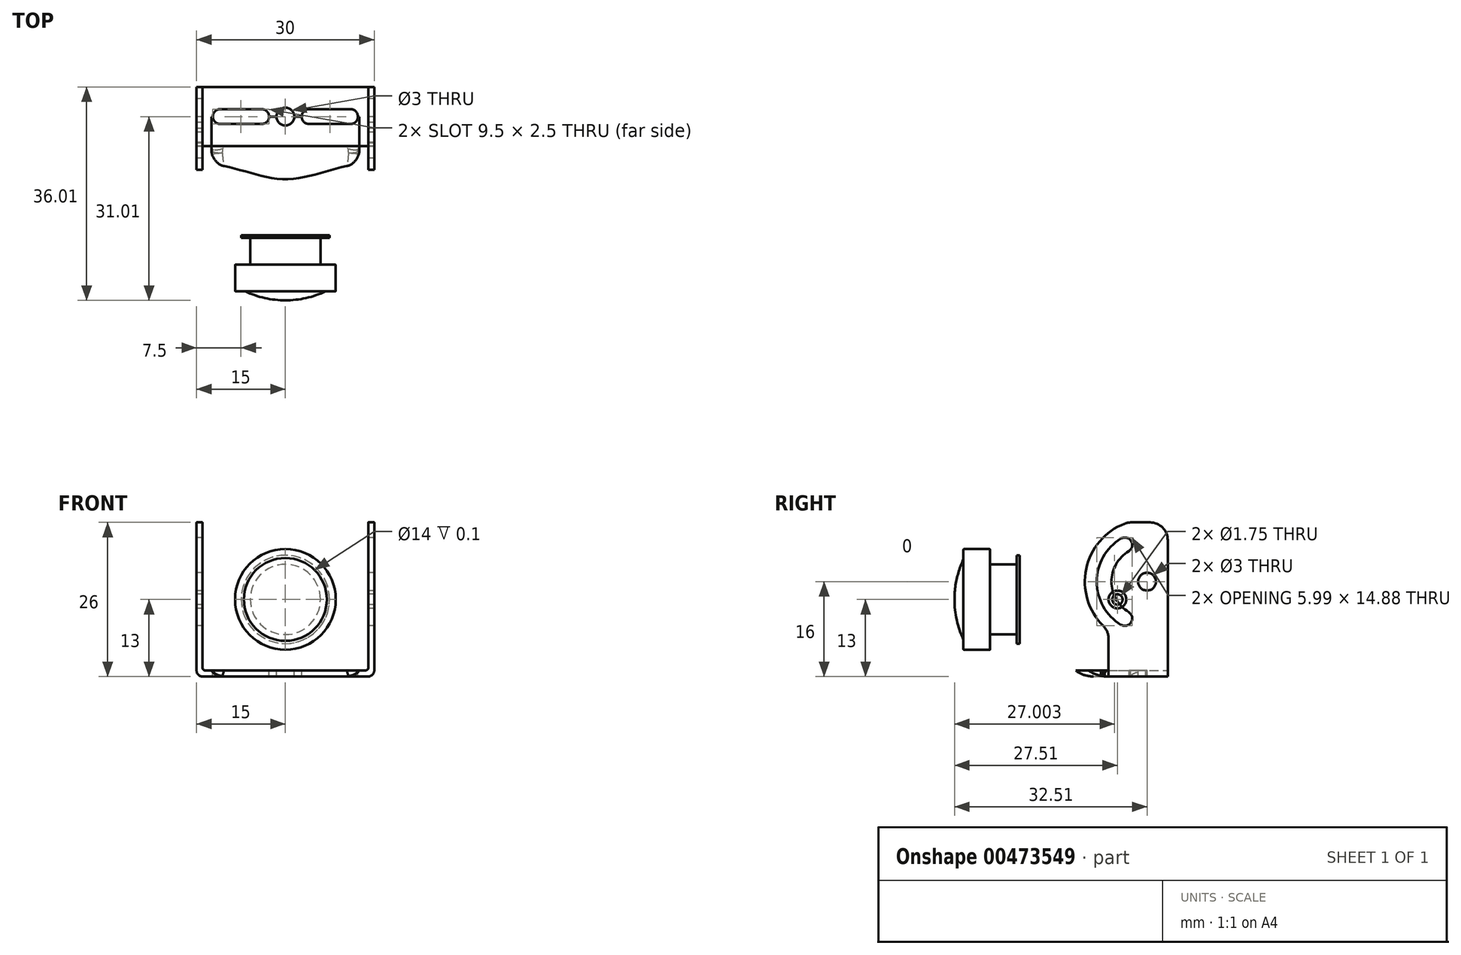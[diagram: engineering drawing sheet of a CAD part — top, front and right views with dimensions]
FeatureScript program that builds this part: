
annotation { "Feature Type Name" : "Feature", "Feature Type Description" : "" }
export const myFeature = defineFeature(function(context is Context, id is Id, definition is map)
    precondition{}
    {
        {
            var Q0;
            Q0=qCreatedBy(makeId("Right.planeOp"),FACE);
            var sketch = newSketch(context, id + "F0", { "sketchPlane" : qUnion([Q0])});
            skLineSegment(sketch, "E0", {"start": v(-18.38, 0) * mm, "end": v(-1.77, 16.62) * mm, "construction": true});
            skLineSegment(sketch, "E1", {"start": v(1.77, 16.62) * mm, "end": v(18.38, 0) * mm, "construction": true});
            skLineSegment(sketch, "E2", {"start": v(18.38, 0) * mm, "end": v(0, -18.38) * mm, "construction": true});
            skLineSegment(sketch, "E3", {"start": v(0, -18.38) * mm, "end": v(-18.38, 0) * mm, "construction": true});
            skArc(sketch, "E4", {"start": v(-5.5, 17.35) * mm, "mid": v(-8.56, 16.3) * mm, "end": v(-10.34, 13.6) * mm});
            skLineSegment(sketch, "E5", {"start": v(-17, 0) * mm, "end": v(-17, 7.32) * mm});
            skArc(sketch, "E6", {"start": v(-16.59, 7.81) * mm, "mid": v(-12.62, 9.8) * mm, "end": v(-10.34, 13.6) * mm});
            skLineSegment(sketch, "E7", {"start": v(0, 0) * mm, "end": v(-17, 0) * mm});
            skPoint(sketch, "E8.visualSharp", {"position": v(0, 18.38) * mm});
            skArc(sketch, "E8.filletArc", {"start": v(1.77, 16.62) * mm, "mid": v(0, 17.35) * mm, "end": v(-1.77, 16.62) * mm, "construction": true});
            skLineSegment(sketch, "E9", {"start": v(0, 17.35) * mm, "end": v(0, 0) * mm});
            skLineSegment(sketch, "E10", {"start": v(0, 17.35) * mm, "end": v(-5.5, 17.35) * mm});
            skPoint(sketch, "E11.visualSharp", {"position": v(-17, 7.75) * mm});
            skArc(sketch, "E11.filletArc", {"start": v(-16.59, 7.81) * mm, "mid": v(-16.88, 7.64) * mm, "end": v(-17, 7.32) * mm});
            skSolve(sketch);
        }
        {
            var Q0;
            Q0=qCreatedBy(makeId("Front.planeOp"),FACE);
            var sketch = newSketch(context, id + "F1", { "sketchPlane" : qUnion([Q0])});
            skLineSegment(sketch, "E12.bottom", {"start": v(10.5, 13) * mm, "end": v(-10.5, 13) * mm});
            skLineSegment(sketch, "E12.top", {"start": v(10.5, -13) * mm, "end": v(-10.5, -13) * mm});
            skLineSegment(sketch, "E12.left", {"start": v(13, 10.5) * mm, "end": v(13, -10.5) * mm});
            skLineSegment(sketch, "E12.right", {"start": v(-13, 10.5) * mm, "end": v(-13, -10.5) * mm});
            skPoint(sketch, "E13.visualSharp", {"position": v(13, 13) * mm});
            skArc(sketch, "E13.filletArc", {"start": v(13, 10.5) * mm, "mid": v(12.27, 12.27) * mm, "end": v(10.5, 13) * mm});
            skPoint(sketch, "E14.visualSharp", {"position": v(-13, 13) * mm});
            skArc(sketch, "E14.filletArc", {"start": v(-10.5, 13) * mm, "mid": v(-12.27, 12.27) * mm, "end": v(-13, 10.5) * mm});
            skPoint(sketch, "E15.visualSharp", {"position": v(13, -13) * mm});
            skArc(sketch, "E15.filletArc", {"start": v(10.5, -13) * mm, "mid": v(12.27, -12.27) * mm, "end": v(13, -10.5) * mm});
            skPoint(sketch, "E16.visualSharp", {"position": v(-13, -13) * mm});
            skArc(sketch, "E16.filletArc", {"start": v(-13, -10.5) * mm, "mid": v(-12.27, -12.27) * mm, "end": v(-10.5, -13) * mm});
            skLineSegment(sketch, "E17.bottom", {"start": v(20, 20) * mm, "end": v(-20, 20) * mm});
            skLineSegment(sketch, "E17.top", {"start": v(20, -20) * mm, "end": v(-20, -20) * mm});
            skLineSegment(sketch, "E17.left", {"start": v(20, 20) * mm, "end": v(20, -20) * mm});
            skLineSegment(sketch, "E17.right", {"start": v(-20, 20) * mm, "end": v(-20, -20) * mm});
            skSolve(sketch);
        }
        {
            var Q0;
            Q0=makeQuery(id+"F0.imprint","IMPRINT",FACE,{"disambiguationData":[TD([[makeQuery(id+"F0.imprint","IMPRINT",EDGE,{"derivedFrom":sQuery(id+"F0.wireOp",EDGE,"E4")}),1.0]])]});
            var Q1;
            Q1=sQuery(id+"F0.wireOp",EDGE,"E7");
            revolve(context, id + "F2", {"entities" : qUnion([Q0]), "axis" : qUnion([Q1]), "revolveType" : RevolveType.FULL});
        }
        {
            var Q0;
            Q0=qSketchRegion(id+"F1",true);
            extrude(context, id + "F3", {"entities" : qUnion([Q0]), "operationType" : NewBodyOperationType.REMOVE, "depth" : 25 * mm});
        }
        {
            var Q0;
            Q0=makeQuery(id+"F3.boolean.opBoolean","INTERSECT",EDGE,{"derivedFrom":[makeQuery(id+"F2.opRevolve","SWEPT_FACE",FACE,{"disambiguationData":[OSD([sQuery(id+"F0.wireOp",EDGE,"E6")])]}),makeQuery(id+"F3.opExtrude","SWEPT_FACE",FACE,{"disambiguationData":[OSD([sQuery(id+"F1.wireOp",EDGE,"E12.left")])]})]});
            var Q1;
            Q1=makeQuery(id+"F3.boolean.opBoolean","INTERSECT",EDGE,{"derivedFrom":[makeQuery(id+"F2.opRevolve","SWEPT_FACE",FACE,{"disambiguationData":[OSD([sQuery(id+"F0.wireOp",EDGE,"E6")])]}),makeQuery(id+"F3.opExtrude","SWEPT_FACE",FACE,{"disambiguationData":[OSD([sQuery(id+"F1.wireOp",EDGE,"E12.top")])]})]});
            var Q2;
            Q2=makeQuery(id+"F3.boolean.opBoolean","INTERSECT",EDGE,{"derivedFrom":[makeQuery(id+"F2.opRevolve","SWEPT_FACE",FACE,{"disambiguationData":[OSD([sQuery(id+"F0.wireOp",EDGE,"E6")])]}),makeQuery(id+"F3.opExtrude","SWEPT_FACE",FACE,{"disambiguationData":[OSD([sQuery(id+"F1.wireOp",EDGE,"E12.right")])]})]});
            var Q3;
            Q3=makeQuery(id+"F3.boolean.opBoolean","INTERSECT",EDGE,{"derivedFrom":[makeQuery(id+"F2.opRevolve","SWEPT_FACE",FACE,{"disambiguationData":[OSD([sQuery(id+"F0.wireOp",EDGE,"E6")])]}),makeQuery(id+"F3.opExtrude","SWEPT_FACE",FACE,{"disambiguationData":[OSD([sQuery(id+"F1.wireOp",EDGE,"E12.bottom")])]})]});
            fillet(context, id + "F4", {"entities" : qUnion([Q0, Q1, Q2, Q3]), "radius" : 5 * mm, "allowEdgeOverflow" : false});
        }
        {
            var Q0;
            {var subQ0=makeQuery(id+"F2.opRevolve","SWEPT_FACE",FACE,{"disambiguationData":[OSD([sQuery(id+"F0.wireOp",EDGE,"E6")])]});var subQ1=makeQuery(id+"F3.opExtrude","SWEPT_FACE",FACE,{"disambiguationData":[OSD([sQuery(id+"F1.wireOp",EDGE,"E12.top")])]});Q0=makeQuery(id+"F4.opFillet","BLEND_EDGE",EDGE,{"blendedFrom":[makeQuery(id+"F3.boolean.opBoolean","INTERSECT",EDGE,{"derivedFrom":[subQ0,subQ1]}),makeQuery(id+"F3.boolean.opBoolean","SPLIT",FACE,{"disambiguationData":[TD([makeQuery(id+"F3.opExtrude","SWEPT_FACE",FACE,{"disambiguationData":[OSD([sQuery(id+"F1.wireOp",EDGE,"E16.filletArc")])]})])],"derivedFrom":makeQuery(id+"F2.opRevolve","SWEPT_FACE",FACE,{"disambiguationData":[OSD([sQuery(id+"F0.wireOp",EDGE,"E4")])]})})],"blendedInto":[makeQuery(id+"F3.boolean.opBoolean","SPLIT",FACE,{"disambiguationData":[TD([makeQuery(id+"F3.opExtrude","SWEPT_FACE",FACE,{"disambiguationData":[OSD([sQuery(id+"F1.wireOp",EDGE,"E16.filletArc")])]})])],"derivedFrom":makeQuery(id+"F2.opRevolve","SWEPT_FACE",FACE,{"disambiguationData":[OSD([sQuery(id+"F0.wireOp",EDGE,"E4")])]})})]});}
            var Q1;
            {var subQ0=makeQuery(id+"F2.opRevolve","SWEPT_FACE",FACE,{"disambiguationData":[OSD([sQuery(id+"F0.wireOp",EDGE,"E6")])]});var subQ1=makeQuery(id+"F3.opExtrude","SWEPT_FACE",FACE,{"disambiguationData":[OSD([sQuery(id+"F1.wireOp",EDGE,"E12.right")])]});Q1=makeQuery(id+"F4.opFillet","BLEND_EDGE",EDGE,{"blendedFrom":[makeQuery(id+"F3.boolean.opBoolean","INTERSECT",EDGE,{"derivedFrom":[subQ0,subQ1]}),makeQuery(id+"F3.boolean.opBoolean","SPLIT",FACE,{"disambiguationData":[TD([makeQuery(id+"F3.opExtrude","SWEPT_FACE",FACE,{"disambiguationData":[OSD([sQuery(id+"F1.wireOp",EDGE,"E16.filletArc")])]})])],"derivedFrom":makeQuery(id+"F2.opRevolve","SWEPT_FACE",FACE,{"disambiguationData":[OSD([sQuery(id+"F0.wireOp",EDGE,"E4")])]})})],"blendedInto":[makeQuery(id+"F3.boolean.opBoolean","SPLIT",FACE,{"disambiguationData":[TD([makeQuery(id+"F3.opExtrude","SWEPT_FACE",FACE,{"disambiguationData":[OSD([sQuery(id+"F1.wireOp",EDGE,"E16.filletArc")])]})])],"derivedFrom":makeQuery(id+"F2.opRevolve","SWEPT_FACE",FACE,{"disambiguationData":[OSD([sQuery(id+"F0.wireOp",EDGE,"E4")])]})})]});}
            var Q2;
            {var subQ0=makeQuery(id+"F2.opRevolve","SWEPT_FACE",FACE,{"disambiguationData":[OSD([sQuery(id+"F0.wireOp",EDGE,"E6")])]});Q2=makeQuery(id+"F4.opFillet","BLEND_EDGE",EDGE,{"blendedFrom":[makeQuery(id+"F3.boolean.opBoolean","INTERSECT",EDGE,{"derivedFrom":[subQ0,makeQuery(id+"F3.opExtrude","SWEPT_FACE",FACE,{"disambiguationData":[OSD([sQuery(id+"F1.wireOp",EDGE,"E12.top")])]})]}),makeQuery(id+"F3.boolean.opBoolean","INTERSECT",EDGE,{"derivedFrom":[subQ0,makeQuery(id+"F3.opExtrude","SWEPT_FACE",FACE,{"disambiguationData":[OSD([sQuery(id+"F1.wireOp",EDGE,"E12.right")])]})]})],"blendedInto":[]});}
            var Q3;
            {var subQ0=makeQuery(id+"F2.opRevolve","SWEPT_FACE",FACE,{"disambiguationData":[OSD([sQuery(id+"F0.wireOp",EDGE,"E6")])]});Q3=makeQuery(id+"F4.opFillet","BLEND_EDGE",EDGE,{"blendedFrom":[makeQuery(id+"F3.boolean.opBoolean","INTERSECT",EDGE,{"derivedFrom":[subQ0,makeQuery(id+"F3.opExtrude","SWEPT_FACE",FACE,{"disambiguationData":[OSD([sQuery(id+"F1.wireOp",EDGE,"E12.bottom")])]})]}),makeQuery(id+"F3.boolean.opBoolean","INTERSECT",EDGE,{"derivedFrom":[subQ0,makeQuery(id+"F3.opExtrude","SWEPT_FACE",FACE,{"disambiguationData":[OSD([sQuery(id+"F1.wireOp",EDGE,"E12.right")])]})]})],"blendedInto":[]});}
            var Q4;
            {var subQ0=makeQuery(id+"F2.opRevolve","SWEPT_FACE",FACE,{"disambiguationData":[OSD([sQuery(id+"F0.wireOp",EDGE,"E6")])]});var subQ1=makeQuery(id+"F3.opExtrude","SWEPT_FACE",FACE,{"disambiguationData":[OSD([sQuery(id+"F1.wireOp",EDGE,"E12.right")])]});Q4=makeQuery(id+"F4.opFillet","BLEND_EDGE",EDGE,{"blendedFrom":[makeQuery(id+"F3.boolean.opBoolean","INTERSECT",EDGE,{"derivedFrom":[subQ0,subQ1]}),makeQuery(id+"F3.boolean.opBoolean","SPLIT",FACE,{"disambiguationData":[TD([makeQuery(id+"F3.opExtrude","SWEPT_FACE",FACE,{"disambiguationData":[OSD([sQuery(id+"F1.wireOp",EDGE,"E14.filletArc")])]})])],"derivedFrom":makeQuery(id+"F2.opRevolve","SWEPT_FACE",FACE,{"disambiguationData":[OSD([sQuery(id+"F0.wireOp",EDGE,"E4")])]})})],"blendedInto":[makeQuery(id+"F3.boolean.opBoolean","SPLIT",FACE,{"disambiguationData":[TD([makeQuery(id+"F3.opExtrude","SWEPT_FACE",FACE,{"disambiguationData":[OSD([sQuery(id+"F1.wireOp",EDGE,"E14.filletArc")])]})])],"derivedFrom":makeQuery(id+"F2.opRevolve","SWEPT_FACE",FACE,{"disambiguationData":[OSD([sQuery(id+"F0.wireOp",EDGE,"E4")])]})})]});}
            var Q5;
            {var subQ0=makeQuery(id+"F2.opRevolve","SWEPT_FACE",FACE,{"disambiguationData":[OSD([sQuery(id+"F0.wireOp",EDGE,"E6")])]});var subQ1=makeQuery(id+"F3.opExtrude","SWEPT_FACE",FACE,{"disambiguationData":[OSD([sQuery(id+"F1.wireOp",EDGE,"E12.bottom")])]});Q5=makeQuery(id+"F4.opFillet","BLEND_EDGE",EDGE,{"blendedFrom":[makeQuery(id+"F3.boolean.opBoolean","INTERSECT",EDGE,{"derivedFrom":[subQ0,subQ1]}),makeQuery(id+"F3.boolean.opBoolean","SPLIT",FACE,{"disambiguationData":[TD([makeQuery(id+"F3.opExtrude","SWEPT_FACE",FACE,{"disambiguationData":[OSD([sQuery(id+"F1.wireOp",EDGE,"E14.filletArc")])]})])],"derivedFrom":makeQuery(id+"F2.opRevolve","SWEPT_FACE",FACE,{"disambiguationData":[OSD([sQuery(id+"F0.wireOp",EDGE,"E4")])]})})],"blendedInto":[makeQuery(id+"F3.boolean.opBoolean","SPLIT",FACE,{"disambiguationData":[TD([makeQuery(id+"F3.opExtrude","SWEPT_FACE",FACE,{"disambiguationData":[OSD([sQuery(id+"F1.wireOp",EDGE,"E14.filletArc")])]})])],"derivedFrom":makeQuery(id+"F2.opRevolve","SWEPT_FACE",FACE,{"disambiguationData":[OSD([sQuery(id+"F0.wireOp",EDGE,"E4")])]})})]});}
            var Q6;
            {var subQ0=makeQuery(id+"F2.opRevolve","SWEPT_FACE",FACE,{"disambiguationData":[OSD([sQuery(id+"F0.wireOp",EDGE,"E6")])]});var subQ1=makeQuery(id+"F3.opExtrude","SWEPT_FACE",FACE,{"disambiguationData":[OSD([sQuery(id+"F1.wireOp",EDGE,"E12.bottom")])]});Q6=makeQuery(id+"F4.opFillet","BLEND_EDGE",EDGE,{"blendedFrom":[makeQuery(id+"F3.boolean.opBoolean","INTERSECT",EDGE,{"derivedFrom":[subQ0,subQ1]}),makeQuery(id+"F3.boolean.opBoolean","SPLIT",FACE,{"disambiguationData":[TD([makeQuery(id+"F3.opExtrude","SWEPT_FACE",FACE,{"disambiguationData":[OSD([sQuery(id+"F1.wireOp",EDGE,"E13.filletArc")])]})])],"derivedFrom":makeQuery(id+"F2.opRevolve","SWEPT_FACE",FACE,{"disambiguationData":[OSD([sQuery(id+"F0.wireOp",EDGE,"E4")])]})})],"blendedInto":[makeQuery(id+"F3.boolean.opBoolean","SPLIT",FACE,{"disambiguationData":[TD([makeQuery(id+"F3.opExtrude","SWEPT_FACE",FACE,{"disambiguationData":[OSD([sQuery(id+"F1.wireOp",EDGE,"E13.filletArc")])]})])],"derivedFrom":makeQuery(id+"F2.opRevolve","SWEPT_FACE",FACE,{"disambiguationData":[OSD([sQuery(id+"F0.wireOp",EDGE,"E4")])]})})]});}
            var Q7;
            {var subQ0=makeQuery(id+"F2.opRevolve","SWEPT_FACE",FACE,{"disambiguationData":[OSD([sQuery(id+"F0.wireOp",EDGE,"E6")])]});var subQ1=makeQuery(id+"F3.opExtrude","SWEPT_FACE",FACE,{"disambiguationData":[OSD([sQuery(id+"F1.wireOp",EDGE,"E12.left")])]});Q7=makeQuery(id+"F4.opFillet","BLEND_EDGE",EDGE,{"blendedFrom":[makeQuery(id+"F3.boolean.opBoolean","INTERSECT",EDGE,{"derivedFrom":[subQ0,subQ1]}),makeQuery(id+"F3.boolean.opBoolean","SPLIT",FACE,{"disambiguationData":[TD([makeQuery(id+"F3.opExtrude","SWEPT_FACE",FACE,{"disambiguationData":[OSD([sQuery(id+"F1.wireOp",EDGE,"E13.filletArc")])]})])],"derivedFrom":makeQuery(id+"F2.opRevolve","SWEPT_FACE",FACE,{"disambiguationData":[OSD([sQuery(id+"F0.wireOp",EDGE,"E4")])]})})],"blendedInto":[makeQuery(id+"F3.boolean.opBoolean","SPLIT",FACE,{"disambiguationData":[TD([makeQuery(id+"F3.opExtrude","SWEPT_FACE",FACE,{"disambiguationData":[OSD([sQuery(id+"F1.wireOp",EDGE,"E13.filletArc")])]})])],"derivedFrom":makeQuery(id+"F2.opRevolve","SWEPT_FACE",FACE,{"disambiguationData":[OSD([sQuery(id+"F0.wireOp",EDGE,"E4")])]})})]});}
            var Q8;
            {var subQ0=makeQuery(id+"F2.opRevolve","SWEPT_FACE",FACE,{"disambiguationData":[OSD([sQuery(id+"F0.wireOp",EDGE,"E6")])]});Q8=makeQuery(id+"F4.opFillet","BLEND_EDGE",EDGE,{"blendedFrom":[makeQuery(id+"F3.boolean.opBoolean","INTERSECT",EDGE,{"derivedFrom":[subQ0,makeQuery(id+"F3.opExtrude","SWEPT_FACE",FACE,{"disambiguationData":[OSD([sQuery(id+"F1.wireOp",EDGE,"E12.bottom")])]})]}),makeQuery(id+"F3.boolean.opBoolean","INTERSECT",EDGE,{"derivedFrom":[subQ0,makeQuery(id+"F3.opExtrude","SWEPT_FACE",FACE,{"disambiguationData":[OSD([sQuery(id+"F1.wireOp",EDGE,"E12.left")])]})]})],"blendedInto":[]});}
            var Q9;
            {var subQ0=makeQuery(id+"F2.opRevolve","SWEPT_FACE",FACE,{"disambiguationData":[OSD([sQuery(id+"F0.wireOp",EDGE,"E6")])]});var subQ1=makeQuery(id+"F3.opExtrude","SWEPT_FACE",FACE,{"disambiguationData":[OSD([sQuery(id+"F1.wireOp",EDGE,"E12.left")])]});Q9=makeQuery(id+"F4.opFillet","BLEND_EDGE",EDGE,{"blendedFrom":[makeQuery(id+"F3.boolean.opBoolean","INTERSECT",EDGE,{"derivedFrom":[subQ0,subQ1]}),makeQuery(id+"F3.boolean.opBoolean","SPLIT",FACE,{"disambiguationData":[TD([makeQuery(id+"F3.opExtrude","SWEPT_FACE",FACE,{"disambiguationData":[OSD([sQuery(id+"F1.wireOp",EDGE,"E15.filletArc")])]})])],"derivedFrom":makeQuery(id+"F2.opRevolve","SWEPT_FACE",FACE,{"disambiguationData":[OSD([sQuery(id+"F0.wireOp",EDGE,"E4")])]})})],"blendedInto":[makeQuery(id+"F3.boolean.opBoolean","SPLIT",FACE,{"disambiguationData":[TD([makeQuery(id+"F3.opExtrude","SWEPT_FACE",FACE,{"disambiguationData":[OSD([sQuery(id+"F1.wireOp",EDGE,"E15.filletArc")])]})])],"derivedFrom":makeQuery(id+"F2.opRevolve","SWEPT_FACE",FACE,{"disambiguationData":[OSD([sQuery(id+"F0.wireOp",EDGE,"E4")])]})})]});}
            var Q10;
            {var subQ0=makeQuery(id+"F2.opRevolve","SWEPT_FACE",FACE,{"disambiguationData":[OSD([sQuery(id+"F0.wireOp",EDGE,"E6")])]});var subQ1=makeQuery(id+"F3.opExtrude","SWEPT_FACE",FACE,{"disambiguationData":[OSD([sQuery(id+"F1.wireOp",EDGE,"E12.top")])]});Q10=makeQuery(id+"F4.opFillet","BLEND_EDGE",EDGE,{"blendedFrom":[makeQuery(id+"F3.boolean.opBoolean","INTERSECT",EDGE,{"derivedFrom":[subQ0,subQ1]}),makeQuery(id+"F3.boolean.opBoolean","SPLIT",FACE,{"disambiguationData":[TD([makeQuery(id+"F3.opExtrude","SWEPT_FACE",FACE,{"disambiguationData":[OSD([sQuery(id+"F1.wireOp",EDGE,"E15.filletArc")])]})])],"derivedFrom":makeQuery(id+"F2.opRevolve","SWEPT_FACE",FACE,{"disambiguationData":[OSD([sQuery(id+"F0.wireOp",EDGE,"E4")])]})})],"blendedInto":[makeQuery(id+"F3.boolean.opBoolean","SPLIT",FACE,{"disambiguationData":[TD([makeQuery(id+"F3.opExtrude","SWEPT_FACE",FACE,{"disambiguationData":[OSD([sQuery(id+"F1.wireOp",EDGE,"E15.filletArc")])]})])],"derivedFrom":makeQuery(id+"F2.opRevolve","SWEPT_FACE",FACE,{"disambiguationData":[OSD([sQuery(id+"F0.wireOp",EDGE,"E4")])]})})]});}
            var Q11;
            {var subQ0=makeQuery(id+"F2.opRevolve","SWEPT_FACE",FACE,{"disambiguationData":[OSD([sQuery(id+"F0.wireOp",EDGE,"E6")])]});Q11=makeQuery(id+"F4.opFillet","BLEND_EDGE",EDGE,{"blendedFrom":[makeQuery(id+"F3.boolean.opBoolean","INTERSECT",EDGE,{"derivedFrom":[subQ0,makeQuery(id+"F3.opExtrude","SWEPT_FACE",FACE,{"disambiguationData":[OSD([sQuery(id+"F1.wireOp",EDGE,"E12.top")])]})]}),makeQuery(id+"F3.boolean.opBoolean","INTERSECT",EDGE,{"derivedFrom":[subQ0,makeQuery(id+"F3.opExtrude","SWEPT_FACE",FACE,{"disambiguationData":[OSD([sQuery(id+"F1.wireOp",EDGE,"E12.left")])]})]})],"blendedInto":[]});}
            fillet(context, id + "F5", {"entities" : qUnion([Q0, Q1, Q2, Q3, Q4, Q5, Q6, Q7, Q8, Q9, Q10, Q11]), "radius" : 2.4 * mm, "allowEdgeOverflow" : false});
        }
        {
            var Q0;
            Q0=makeQuery(id+"F2.opRevolve","SWEPT_FACE",FACE,{"disambiguationData":[OSD([sQuery(id+"F0.wireOp",EDGE,"E9")])]});
            var sketch = newSketch(context, id + "F6", { "sketchPlane" : qUnion([Q0])});
            skLineSegment(sketch, "E18.bottom", {"start": v(-10.5, 12) * mm, "end": v(10.5, 12) * mm});
            skLineSegment(sketch, "E18.top", {"start": v(-10.5, -12) * mm, "end": v(1, -12) * mm});
            skLineSegment(sketch, "E18.left", {"start": v(-12, 10.5) * mm, "end": v(-12, -10.5) * mm});
            skLineSegment(sketch, "E18.right", {"start": v(12, 10.5) * mm, "end": v(12, -8) * mm});
            skPoint(sketch, "E19.visualSharp", {"position": v(-12, 12) * mm});
            skArc(sketch, "E19.filletArc", {"start": v(-10.5, 12) * mm, "mid": v(-11.56, 11.56) * mm, "end": v(-12, 10.5) * mm});
            skPoint(sketch, "E20.visualSharp", {"position": v(-12, -12) * mm});
            skArc(sketch, "E20.filletArc", {"start": v(-12, -10.5) * mm, "mid": v(-11.56, -11.56) * mm, "end": v(-10.5, -12) * mm});
            skPoint(sketch, "E21.visualSharp", {"position": v(12, 12) * mm});
            skArc(sketch, "E21.filletArc", {"start": v(12, 10.5) * mm, "mid": v(11.56, 11.56) * mm, "end": v(10.5, 12) * mm});
            skPoint(sketch, "E22.visualSharp", {"position": v(12, -12) * mm});
            skLineSegment(sketch, "E23", {"start": v(1, -12) * mm, "end": v(1, -8) * mm});
            skLineSegment(sketch, "E24", {"start": v(1, -8) * mm, "end": v(12, -8) * mm});
            skCircle(sketch, "E25", {"center": v(-10, -10) * mm, "radius": 1.4 * mm});
            skCircle(sketch, "E26", {"center": v(10, 10) * mm, "radius": 1.4 * mm});
            skSolve(sketch);
        }
        {
            var Q0;
            Q0=makeQuery(id+"F6.imprint","IMPRINT",FACE,{"disambiguationData":[TD([[makeQuery(id+"F6.imprint","IMPRINT",EDGE,{"derivedFrom":sQuery(id+"F6.wireOp",EDGE,"E18.bottom")}),-1.0]])]});
            var Q1;
            Q1=makeQuery(id+"F6.imprint","IMPRINT",FACE,{"disambiguationData":[TD([[makeQuery(id+"F6.imprint","IMPRINT",EDGE,{"derivedFrom":sQuery(id+"F6.wireOp",EDGE,"E26")}),1.0]])]});
            var Q2;
            Q2=makeQuery(id+"F6.imprint","IMPRINT",FACE,{"disambiguationData":[TD([[makeQuery(id+"F6.imprint","IMPRINT",EDGE,{"derivedFrom":sQuery(id+"F6.wireOp",EDGE,"E25")}),1.0]])]});
            extrude(context, id + "F7", {"entities" : qUnion([Q0, Q1, Q2]), "operationType" : NewBodyOperationType.REMOVE, "oppositeDirection" : true, "depth" : 0.1 * mm});
        }
        {
            var Q0;
            Q0=makeQuery(id+"F6.imprint","IMPRINT",FACE,{"disambiguationData":[TD([[makeQuery(id+"F6.imprint","IMPRINT",EDGE,{"derivedFrom":sQuery(id+"F6.wireOp",EDGE,"E26")}),1.0]])]});
            var Q1;
            Q1=makeQuery(id+"F6.imprint","IMPRINT",FACE,{"disambiguationData":[TD([[makeQuery(id+"F6.imprint","IMPRINT",EDGE,{"derivedFrom":sQuery(id+"F6.wireOp",EDGE,"E25")}),1.0]])]});
            extrude(context, id + "F8", {"entities" : qUnion([Q0, Q1]), "operationType" : NewBodyOperationType.REMOVE, "oppositeDirection" : true, "depth" : 0.3 * mm});
        }
        {
            var Q0;
            Q0=makeQuery(id+"F8.boolean.opBoolean","INTERSECT",EDGE,{"derivedFrom":[makeQuery(id+"F7.boolean.opBoolean","COPY",FACE,{"derivedFrom":makeQuery(id+"F7.opExtrude","CAP_FACE",FACE,{"disambiguationData":[OSD([sQuery(id+"F6.wireOp",EDGE,"E18.bottom"),sQuery(id+"F6.wireOp",EDGE,"E18.top"),sQuery(id+"F6.wireOp",EDGE,"E18.left"),sQuery(id+"F6.wireOp",EDGE,"E18.right"),sQuery(id+"F6.wireOp",EDGE,"E19.filletArc"),sQuery(id+"F6.wireOp",EDGE,"E20.filletArc"),sQuery(id+"F6.wireOp",EDGE,"E21.filletArc"),sQuery(id+"F6.wireOp",EDGE,"E23"),sQuery(id+"F6.wireOp",EDGE,"E24")])],"isStart":false})}),makeQuery(id+"F8.opExtrude","SWEPT_FACE",FACE,{"disambiguationData":[OSD([sQuery(id+"F6.wireOp",EDGE,"E26")])]})]});
            var Q1;
            Q1=makeQuery(id+"F8.boolean.opBoolean","INTERSECT",EDGE,{"derivedFrom":[makeQuery(id+"F7.boolean.opBoolean","COPY",FACE,{"derivedFrom":makeQuery(id+"F7.opExtrude","CAP_FACE",FACE,{"disambiguationData":[OSD([sQuery(id+"F6.wireOp",EDGE,"E18.bottom"),sQuery(id+"F6.wireOp",EDGE,"E18.top"),sQuery(id+"F6.wireOp",EDGE,"E18.left"),sQuery(id+"F6.wireOp",EDGE,"E18.right"),sQuery(id+"F6.wireOp",EDGE,"E19.filletArc"),sQuery(id+"F6.wireOp",EDGE,"E20.filletArc"),sQuery(id+"F6.wireOp",EDGE,"E21.filletArc"),sQuery(id+"F6.wireOp",EDGE,"E23"),sQuery(id+"F6.wireOp",EDGE,"E24")])],"isStart":false})}),makeQuery(id+"F8.opExtrude","SWEPT_FACE",FACE,{"disambiguationData":[OSD([sQuery(id+"F6.wireOp",EDGE,"E25")])]})]});
            chamfer(context, id + "F9", {"entities" : qUnion([Q0, Q1]), "width" : 0.1 * mm, "tangentPropagation" : true});
        }
        {
            var Q0;
            Q0=makeQuery(id+"F2.opRevolve","SWEPT_FACE",FACE,{"disambiguationData":[OSD([sQuery(id+"F0.wireOp",EDGE,"E9")])]});
            var sketch = newSketch(context, id + "F10", { "sketchPlane" : qUnion([Q0])});
            skLineSegment(sketch, "E27.bottom", {"start": v(1, -8) * mm, "end": v(10.9, -8) * mm});
            skLineSegment(sketch, "E27.top", {"start": v(1, -11.3) * mm, "end": v(10.9, -11.3) * mm});
            skLineSegment(sketch, "E27.left", {"start": v(1, -8) * mm, "end": v(1, -11.3) * mm});
            skLineSegment(sketch, "E27.right", {"start": v(10.9, -8) * mm, "end": v(10.9, -11.3) * mm});
            skSolve(sketch);
        }
        {
            var Q0;
            Q0=qSketchRegion(id+"F10",true);
            extrude(context, id + "F11", {"entities" : qUnion([Q0]), "operationType" : NewBodyOperationType.ADD, "depth" : 1.6 * mm});
        }
        {
            var Q0;
            Q0=makeQuery(id+"F2.opRevolve","SWEPT_FACE",FACE,{"disambiguationData":[OSD([sQuery(id+"F0.wireOp",EDGE,"E5")])]});
            var sketch = newSketch(context, id + "F12", { "sketchPlane" : qUnion([Q0])});
            skCircle(sketch, "E28", {"center": v(0, 0) * mm, "radius": 5.92 * mm});
            skSolve(sketch);
        }
        {
            var Q0;
            Q0=makeQuery(id+"F12.imprint","IMPRINT",FACE,{"disambiguationData":[TD([[makeQuery(id+"F12.imprint","IMPRINT",EDGE,{"derivedFrom":sQuery(id+"F12.wireOp",EDGE,"E28")}),1.0]])]});
            extrude(context, id + "F13", {"entities" : qUnion([Q0]), "operationType" : NewBodyOperationType.REMOVE, "oppositeDirection" : true, "depth" : 12 * mm});
        }
        {
            var Q0;
            Q0=qCreatedBy(makeId("Right.planeOp"),FACE);
            var sketch = newSketch(context, id + "F14", { "sketchPlane" : qUnion([Q0])});
            skArc(sketch, "E29", {"start": v(-3.6, 2.5) * mm, "mid": v(-6, 0) * mm, "end": v(-3.6, -2.5) * mm});
            skLineSegment(sketch, "E30", {"start": v(-3.6, 2.5) * mm, "end": v(0, 2.65) * mm});
            skLineSegment(sketch, "E31", {"start": v(-3.6, -2.5) * mm, "end": v(0, -2.65) * mm});
            skLineSegment(sketch, "E32", {"start": v(0, -2.65) * mm, "end": v(0, 2.65) * mm});
            skSolve(sketch);
        }
        {
            var Q0;
            Q0=qSketchRegion(id+"F14",true);
            extrude(context, id + "F15", {"entities" : qUnion([Q0]), "operationType" : NewBodyOperationType.ADD, "endBound" : BoundingType.SYMMETRIC, "depth" : 26.25 * mm});
        }
        {
            var Q0;
            Q0=qCreatedBy(makeId("Right.planeOp"),FACE);
            var sketch = newSketch(context, id + "F16", { "sketchPlane" : qUnion([Q0])});
            skCircle(sketch, "E33", {"center": v(-3.5, 0) * mm, "radius": 2 * mm});
            skSolve(sketch);
        }
        {
            var Q0;
            Q0=qSketchRegion(id+"F16",true);
            extrude(context, id + "F17", {"entities" : qUnion([Q0]), "operationType" : NewBodyOperationType.ADD, "endBound" : BoundingType.SYMMETRIC, "depth" : 28 * mm});
        }
        {
            var Q0;
            Q0=qCreatedBy(makeId("Right.planeOp"),FACE);
            var sketch = newSketch(context, id + "F18", { "sketchPlane" : qUnion([Q0])});
            skCircle(sketch, "E34", {"center": v(-3.5, 0) * mm, "radius": 1.5 * mm});
            skCircle(sketch, "E35", {"center": v(-3.5, 0) * mm, "radius": 0.88 * mm});
            skSolve(sketch);
        }
        {
            var Q0;
            Q0=qSketchRegion(id+"F18",true);
            extrude(context, id + "F19", {"entities" : qUnion([Q0]), "operationType" : NewBodyOperationType.ADD, "endBound" : BoundingType.SYMMETRIC, "depth" : 30 * mm});
        }
        {
            var Q0;
            Q0=makeQuery(id+"F15.boolean.opBoolean","MERGE",FACE,{"derivedFrom":[makeQuery(id+"F2.opRevolve","SWEPT_FACE",FACE,{"disambiguationData":[OSD([sQuery(id+"F0.wireOp",EDGE,"E9")])]}),makeQuery(id+"F15.opExtrude","SWEPT_FACE",FACE,{"disambiguationData":[OSD([sQuery(id+"F14.wireOp",EDGE,"E32")])]})]});
            var sketch = newSketch(context, id + "F20", { "sketchPlane" : qUnion([Q0])});
            skLineSegment(sketch, "E36.bottom", {"start": v(-12, 2.65) * mm, "end": v(12, 2.65) * mm});
            skLineSegment(sketch, "E36.top", {"start": v(-12, -2.65) * mm, "end": v(12, -2.65) * mm});
            skLineSegment(sketch, "E36.left", {"start": v(-12, 2.65) * mm, "end": v(-12, -2.65) * mm});
            skLineSegment(sketch, "E36.right", {"start": v(12, 2.65) * mm, "end": v(12, -2.65) * mm});
            skSolve(sketch);
        }
        {
            var Q0;
            Q0=makeQuery(id+"F20.imprint","IMPRINT",FACE,{"disambiguationData":[TD([[makeQuery(id+"F20.imprint","IMPRINT",EDGE,{"derivedFrom":sQuery(id+"F20.wireOp",EDGE,"E36.bottom")}),-1.0]])]});
            extrude(context, id + "F21", {"entities" : qUnion([Q0]), "operationType" : NewBodyOperationType.REMOVE, "oppositeDirection" : true, "depth" : 0.1 * mm});
        }
        {
            var Q0;
            Q0=makeQuery(id+"F2.opRevolve","SWEPT_FACE",FACE,{"disambiguationData":[OSD([sQuery(id+"F0.wireOp",EDGE,"E5")])]});
            var sketch = newSketch(context, id + "F22", { "sketchPlane" : qUnion([Q0])});
            skCircle(sketch, "E37", {"center": v(0, 0) * mm, "radius": 7.45 * mm});
            skSolve(sketch);
        }
        {
            var Q0;
            Q0=qSketchRegion(id+"F22",true);
            extrude(context, id + "F23", {"entities" : qUnion([Q0]), "operationType" : NewBodyOperationType.ADD, "depth" : 3.5 * mm});
        }
        {
            var Q0;
            Q0=makeQuery(id+"F23.opExtrude","CAP_FACE",FACE,{"disambiguationData":[OSD([sQuery(id+"F22.wireOp",EDGE,"E37")])],"isStart":false});
            var sketch = newSketch(context, id + "F24", { "sketchPlane" : qUnion([Q0])});
            skCircle(sketch, "E38", {"center": v(0, 0) * mm, "radius": 5.92 * mm});
            skSolve(sketch);
        }
        {
            var Q0;
            Q0=makeQuery(id+"F24.imprint","IMPRINT",FACE,{"disambiguationData":[TD([[makeQuery(id+"F24.imprint","IMPRINT",EDGE,{"derivedFrom":sQuery(id+"F24.wireOp",EDGE,"E38")}),1.0]])]});
            extrude(context, id + "F25", {"entities" : qUnion([Q0]), "operationType" : NewBodyOperationType.ADD, "depth" : 4.5 * mm});
        }
        {
            var Q0;
            Q0=makeQuery(id+"F25.opExtrude","CAP_FACE",FACE,{"disambiguationData":[OSD([sQuery(id+"F24.wireOp",EDGE,"E38")])],"isStart":false});
            var sketch = newSketch(context, id + "F26", { "sketchPlane" : qUnion([Q0])});
            skCircle(sketch, "E39", {"center": v(0, 0) * mm, "radius": 8.5 * mm});
            skSolve(sketch);
        }
        {
            var Q0;
            Q0=qSketchRegion(id+"F26",true);
            extrude(context, id + "F27", {"entities" : qUnion([Q0]), "operationType" : NewBodyOperationType.ADD, "depth" : 4.5 * mm});
        }
        {
            var Q0;
            Q0=makeQuery(id+"F27.opExtrude","CAP_FACE",FACE,{"disambiguationData":[OSD([sQuery(id+"F26.wireOp",EDGE,"E39")])],"isStart":false});
            var sketch = newSketch(context, id + "F28", { "sketchPlane" : qUnion([Q0])});
            skCircle(sketch, "E40", {"center": v(0, 0) * mm, "radius": 7 * mm});
            skSolve(sketch);
        }
        {
            var Q0;
            Q0=makeQuery(id+"F28.imprint","IMPRINT",FACE,{"disambiguationData":[TD([[makeQuery(id+"F28.imprint","IMPRINT",EDGE,{"derivedFrom":sQuery(id+"F28.wireOp",EDGE,"E40")}),1.0]])]});
            extrude(context, id + "F29", {"entities" : qUnion([Q0]), "operationType" : NewBodyOperationType.REMOVE, "oppositeDirection" : true, "depth" : 0.1 * mm});
        }
        {
            var Q0;
            Q0=qCreatedBy(makeId("Right.planeOp"),FACE);
            var sketch = newSketch(context, id + "F30", { "sketchPlane" : qUnion([Q0])});
            skLineSegment(sketch, "E41", {"start": v(-29.4, 0) * mm, "end": v(-29.4, 7) * mm});
            skArc(sketch, "E42", {"start": v(-29.4, 7) * mm, "mid": v(-30.6, 3.6) * mm, "end": v(-31.01, 0) * mm});
            skLineSegment(sketch, "E43", {"start": v(-29.4, 0) * mm, "end": v(-31.01, 0) * mm});
            skPoint(sketch, "E44.orphan", {"position": v(-29.4, -7) * mm});
            skSolve(sketch);
        }
        {
            var Q0;
            Q0=qSketchRegion(id+"F30",true);
            var Q1;
            Q1=sQuery(id+"F30.wireOp",EDGE,"E43");
            revolve(context, id + "F31", {"operationType" : NewBodyOperationType.ADD, "entities" : qUnion([Q0]), "axis" : qUnion([Q1]), "revolveType" : RevolveType.FULL});
        }
        {
            var Q0;
            Q0=qCreatedBy(makeId("Right.planeOp"),FACE);
            var sketch = newSketch(context, id + "F32", { "sketchPlane" : qUnion([Q0])});
            skLineSegment(sketch, "E45.bottom", {"start": v(-19.25, 7.5) * mm, "end": v(-18.25, 7.5) * mm});
            skLineSegment(sketch, "E45.top", {"start": v(-19.25, 7) * mm, "end": v(-18.25, 7) * mm});
            skLineSegment(sketch, "E45.left", {"start": v(-19.25, 7.5) * mm, "end": v(-19.25, 7) * mm});
            skLineSegment(sketch, "E45.right", {"start": v(-18.25, 7.5) * mm, "end": v(-18.25, 7) * mm});
            skSolve(sketch);
        }
        {
            var Q0;
            Q0=qSketchRegion(id+"F32",true);
            var Q1;
            Q1=sQuery(id+"F30.wireOp",EDGE,"E43");
            revolve(context, id + "F33", {"operationType" : NewBodyOperationType.REMOVE, "entities" : qUnion([Q0]), "axis" : qUnion([Q1]), "revolveType" : RevolveType.FULL, "oppositeDirection" : true});
        }
        {
            var Q0;
            Q0=makeQuery(id+"F27.opExtrude","CAP_EDGE",EDGE,{"disambiguationData":[OSD([sQuery(id+"F26.wireOp",EDGE,"E39")])],"isStart":false});
            var Q1;
            Q1=makeQuery(id+"F27.opExtrude","CAP_EDGE",EDGE,{"disambiguationData":[OSD([sQuery(id+"F26.wireOp",EDGE,"E39")])],"isStart":true});
            fillet(context, id + "F34", {"entities" : qUnion([Q0, Q1]), "radius" : 0.1 * mm, "tangentPropagation" : true, "allowEdgeOverflow" : false});
        }
        {
            var Q0;
            Q0=qCreatedBy(makeId("Right.planeOp"),FACE);
            var sketch = newSketch(context, id + "F35", { "sketchPlane" : qUnion([Q0])});
            skLineSegment(sketch, "E46.bottom", {"start": v(5, -13) * mm, "end": v(-5, -13) * mm});
            skLineSegment(sketch, "E46.top", {"start": v(2, 13) * mm, "end": v(-1.2, 13) * mm});
            skLineSegment(sketch, "E46.left", {"start": v(5, -13) * mm, "end": v(5, 10) * mm});
            skLineSegment(sketch, "E46.right", {"start": v(-5, -13) * mm, "end": v(-5, -6.6) * mm});
            skCircle(sketch, "E47", {"center": v(1.5, 3) * mm, "radius": 1.5 * mm});
            skArc(sketch, "E48", {"start": v(-1.6, 8.14) * mm, "mid": v(-4.5, 3) * mm, "end": v(-1.6, -2.14) * mm});
            skArc(sketch, "E49", {"start": v(-2.9, 10.27) * mm, "mid": v(-7, 3) * mm, "end": v(-2.9, -4.27) * mm});
            skArc(sketch, "E50", {"start": v(-2.27, 12.8) * mm, "mid": v(-8.78, 5.15) * mm, "end": v(-5.89, -4.46) * mm});
            skCircle(sketch, "E51", {"center": v(1.5, 3) * mm, "radius": 7.25 * mm, "construction": true});
            skArc(sketch, "E52", {"start": v(-1.6, 8.14) * mm, "mid": v(-1.18, 9.85) * mm, "end": v(-2.9, 10.27) * mm});
            skArc(sketch, "E53", {"start": v(-2.9, -4.27) * mm, "mid": v(-1.18, -3.85) * mm, "end": v(-1.6, -2.14) * mm});
            skPoint(sketch, "E54.visualSharp", {"position": v(5, 13) * mm});
            skArc(sketch, "E54.filletArc", {"start": v(5, 10) * mm, "mid": v(4.12, 12.12) * mm, "end": v(2, 13) * mm});
            skPoint(sketch, "E55.visualSharp", {"position": v(-1.7, 13) * mm});
            skArc(sketch, "E55.filletArc", {"start": v(-1.2, 13) * mm, "mid": v(-1.74, 12.95) * mm, "end": v(-2.27, 12.8) * mm});
            skPoint(sketch, "E56.visualSharp", {"position": v(-5, -5.25) * mm});
            skArc(sketch, "E56.filletArc", {"start": v(-5, -6.6) * mm, "mid": v(-5.23, -5.44) * mm, "end": v(-5.89, -4.46) * mm});
            skSolve(sketch);
        }
        {
            var Q0;
            Q0=makeQuery(id+"F35.imprint","IMPRINT",FACE,{"disambiguationData":[TD([[makeQuery(id+"F35.imprint","IMPRINT",EDGE,{"derivedFrom":sQuery(id+"F35.wireOp",EDGE,"E46.bottom")}),-1.0]])]});
            extrude(context, id + "F36", {"entities" : qUnion([Q0]), "endBound" : BoundingType.SYMMETRIC, "depth" : 30 * mm});
        }
        {
            var Q0;
            Q0=makeQuery(id+"F36.opExtrude","SWEPT_FACE",FACE,{"disambiguationData":[OSD([sQuery(id+"F35.wireOp",EDGE,"E46.left")])]});
            var sketch = newSketch(context, id + "F37", { "sketchPlane" : qUnion([Q0])});
            skLineSegment(sketch, "E57.bottom", {"start": v(-14, 14) * mm, "end": v(14, 14) * mm});
            skLineSegment(sketch, "E57.top", {"start": v(-13.5, -12) * mm, "end": v(13.5, -12) * mm});
            skLineSegment(sketch, "E57.left", {"start": v(-14, 14) * mm, "end": v(-14, -11.5) * mm});
            skLineSegment(sketch, "E57.right", {"start": v(14, 14) * mm, "end": v(14, -11.5) * mm});
            skPoint(sketch, "E58.visualSharp", {"position": v(-14, -12) * mm});
            skArc(sketch, "E58.filletArc", {"start": v(-14, -11.5) * mm, "mid": v(-13.85, -11.85) * mm, "end": v(-13.5, -12) * mm});
            skPoint(sketch, "E59.visualSharp", {"position": v(14, -12) * mm});
            skArc(sketch, "E59.filletArc", {"start": v(13.5, -12) * mm, "mid": v(13.85, -11.85) * mm, "end": v(14, -11.5) * mm});
            skSolve(sketch);
        }
        {
            var Q0;
            Q0=qSketchRegion(id+"F37",true);
            extrude(context, id + "F38", {"entities" : qUnion([Q0]), "operationType" : NewBodyOperationType.REMOVE, "oppositeDirection" : true, "depth" : 25 * mm});
        }
        {
            var Q0;
            Q0=makeQuery(id+"F36.opExtrude","CAP_EDGE",EDGE,{"disambiguationData":[OSD([sQuery(id+"F35.wireOp",EDGE,"E46.bottom")])],"isStart":false});
            var Q1;
            Q1=makeQuery(id+"F36.opExtrude","CAP_EDGE",EDGE,{"disambiguationData":[OSD([sQuery(id+"F35.wireOp",EDGE,"E46.bottom")])],"isStart":true});
            fillet(context, id + "F39", {"entities" : qUnion([Q0, Q1]), "radius" : 1 * mm, "tangentPropagation" : true, "allowEdgeOverflow" : false});
        }
        {
            var Q0;
            Q0=makeQuery(id+"F38.boolean.opBoolean","COPY",FACE,{"derivedFrom":makeQuery(id+"F38.opExtrude","SWEPT_FACE",FACE,{"disambiguationData":[OSD([sQuery(id+"F37.wireOp",EDGE,"E57.top")])]})});
            var sketch = newSketch(context, id + "F40", { "sketchPlane" : qUnion([Q0])});
            skCircle(sketch, "E60", {"center": v(0, 0) * mm, "radius": 1.5 * mm});
            skLineSegment(sketch, "E61", {"start": v(-11, 0) * mm, "end": v(-4, 0) * mm, "construction": true});
            skLineSegment(sketch, "E62.MirrorCS", {"start": v(11, 0) * mm, "end": v(4, 0) * mm, "construction": true});
            skArc(sketch, "E63.0.startCap", {"start": v(-11, -1.25) * mm, "mid": v(-12.25, 0) * mm, "end": v(-11, 1.25) * mm});
            skArc(sketch, "E63.0.endCap", {"start": v(-4, 1.25) * mm, "mid": v(-2.75, 0) * mm, "end": v(-4, -1.25) * mm});
            skLineSegment(sketch, "E63.0.left", {"start": v(-11, 1.25) * mm, "end": v(-4, 1.25) * mm});
            skLineSegment(sketch, "E63.0.right", {"start": v(-11, -1.25) * mm, "end": v(-4, -1.25) * mm});
            skArc(sketch, "E63.1.startCap", {"start": v(11, 1.25) * mm, "mid": v(12.25, 0) * mm, "end": v(11, -1.25) * mm});
            skArc(sketch, "E63.1.endCap", {"start": v(4, -1.25) * mm, "mid": v(2.75, 0) * mm, "end": v(4, 1.25) * mm});
            skLineSegment(sketch, "E63.1.left", {"start": v(11, -1.25) * mm, "end": v(4, -1.25) * mm});
            skLineSegment(sketch, "E63.1.right", {"start": v(11, 1.25) * mm, "end": v(4, 1.25) * mm});
            skSolve(sketch);
        }
        {
            var Q0;
            Q0=qSketchRegion(id+"F40",true);
            extrude(context, id + "F41", {"entities" : qUnion([Q0]), "operationType" : NewBodyOperationType.REMOVE, "oppositeDirection" : true, "depth" : 25 * mm});
        }
    });
